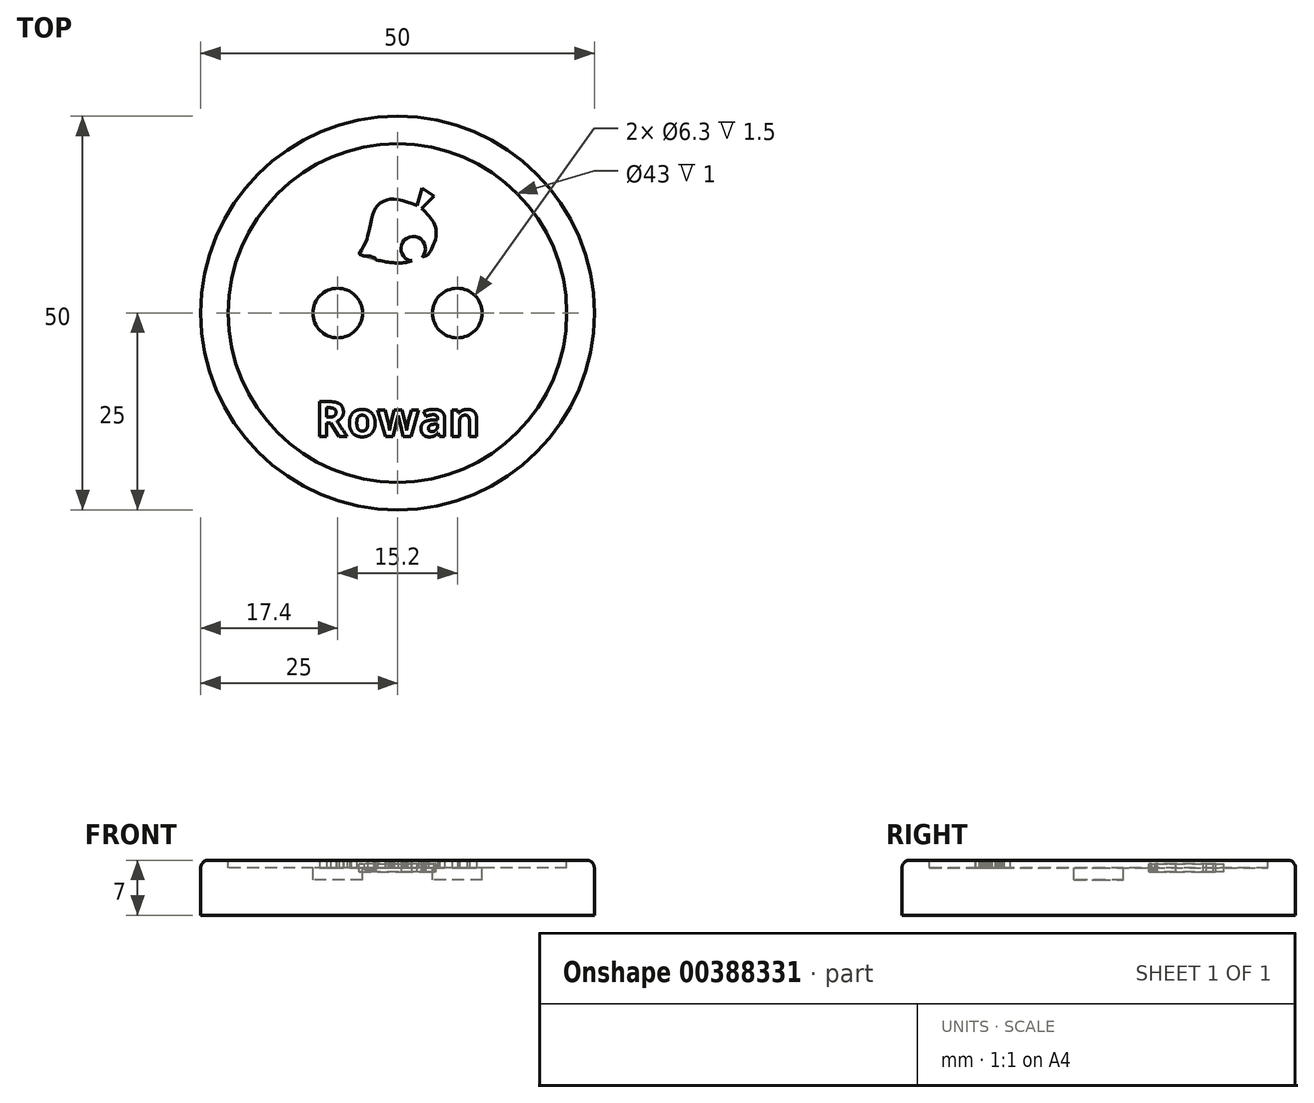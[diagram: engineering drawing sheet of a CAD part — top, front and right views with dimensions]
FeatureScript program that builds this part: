
annotation { "Feature Type Name" : "Feature", "Feature Type Description" : "" }
export const myFeature = defineFeature(function(context is Context, id is Id, definition is map)
    precondition{}
    {
        {
            var Q0;
            Q0=qCreatedBy(makeId("Top.planeOp"),FACE);
            var sketch = newSketch(context, id + "F0", { "sketchPlane" : qUnion([Q0])});
            skCircle(sketch, "E0", {"center": v(0, 0) * mm, "radius": 25 * mm});
            skSolve(sketch);
        }
        {
            var Q0;
            Q0 = qSketchRegion(id + "F0", true);
            extrude(context, id + "F1", {"entities" : qUnion([Q0]), "depth" : 7 * mm});
        }
        {
            var Q0;
            Q0=makeQuery(id+"F1.opExtrude","CAP_FACE",FACE,{"disambiguationData":[OSD([sQuery(id+"F0.wireOp",EDGE,"E0")])],"isStart":false});
            var sketch = newSketch(context, id + "F2", { "sketchPlane" : qUnion([Q0])});
            skLineSegment(sketch, "E1", {"start": v(6.19, 20.35) * mm, "end": v(4.91, 15.94) * mm});
            skLineSegment(sketch, "E2", {"start": v(6.19, 20.35) * mm, "end": v(9.23, 18.39) * mm});
            skFitSpline(sketch, "E3", {"points": [v(4.91, 15.94) * mm, v(0.1, 17.5) * mm, v(-2.94, 17.3) * mm, v(-5, 15.94) * mm, v(-6.27, 13.68) * mm, v(-7.25, 9.46) * mm, v(-7.94, 7) * mm, v(-9.7, 3.57) * mm], "startDerivative": vector(-28.59, 11.34) * mm, "endDerivative": vector(-13.25, -23.76) * mm});
            skFitSpline(sketch, "E4", {"points": [v(-9.7, 3.57) * mm, v(-5.98, 2.3) * mm, v(-1.27, 1.42) * mm, v(1.67, 1.42) * mm, v(3.73, 1.9) * mm], "startDerivative": vector(13.08, -5) * mm, "endDerivative": vector(10.07, 2.94) * mm});
            skFitSpline(sketch, "E5", {"points": [v(3.73, 1.9) * mm, v(2.26, 2.3) * mm, v(1.08, 3.97) * mm, v(1.08, 6.03) * mm, v(2.46, 7.7) * mm, v(4.91, 7.99) * mm, v(6.68, 6.52) * mm, v(7.07, 4.79) * mm, v(6.38, 2.89) * mm], "startDerivative": vector(-14.18, 1.44) * mm, "endDerivative": vector(-7.37, -15.3) * mm});
            skFitSpline(sketch, "E6", {"points": [v(6.38, 2.89) * mm, v(7.76, 3.57) * mm, v(9.23, 6.13) * mm, v(9.82, 9.46) * mm, v(8.64, 12.5) * mm, v(6.09, 15.2) * mm], "startDerivative": vector(9.78, 3.1) * mm, "endDerivative": vector(-12.34, 11.35) * mm});
            skLineSegment(sketch, "E7", {"start": v(6.09, 15.2) * mm, "end": v(9.23, 18.39) * mm});
            skSolve(sketch);
        }
        {
            var Q0;
            Q0 = qSketchRegion(id + "F2", true);
            extrude(context, id + "F3", {"entities" : qUnion([Q0]), "oppositeDirection" : true, "depth" : 3 * mm});
        }
        {
            var Q0;
            Q0=makeQuery(id+"F1.opExtrude","CAP_FACE",FACE,{"disambiguationData":[OSD([sQuery(id+"F0.wireOp",EDGE,"E0")])],"isStart":false});
            var sketch = newSketch(context, id + "F4", { "sketchPlane" : qUnion([Q0])});
            skCircle(sketch, "E8", {"center": v(0, 0) * mm, "radius": 21.5 * mm});
            skSolve(sketch);
        }
        {
            var Q0;
            Q0 = qSketchRegion(id + "F4", true);
            extrude(context, id + "F5", {"entities" : qUnion([Q0]), "operationType" : NewBodyOperationType.REMOVE, "oppositeDirection" : true, "depth" : 1 * mm});
        }
        {
            var Q0;
            Q0=makeQuery(id+"F1.opExtrude","CAP_EDGE",EDGE,{"disambiguationData":[OSD([sQuery(id+"F0.wireOp",EDGE,"E0")])],"isStart":false});
            fillet(context, id + "F6", {"entities" : qUnion([Q0]), "radius" : 1 * mm, "tangentPropagation" : true, "allowEdgeOverflow" : false});
        }
        {
            var Q0;
            Q0=makeQuery(id+"F5.boolean.opBoolean","COPY",FACE,{"derivedFrom":makeQuery(id+"F5.opExtrude","CAP_FACE",FACE,{"disambiguationData":[OSD([sQuery(id+"F4.wireOp",EDGE,"E8")])],"isStart":false})});
            var sketch = newSketch(context, id + "F7", { "sketchPlane" : qUnion([Q0])});
            skText(sketch, "E9", { "text": "Rowan", "fontName": "OpenSans-Bold.ttf"});
            const initialGuessF7  = {"E9": [-0.01047, -0.01567, 1, 0, 0.00445]};
            skSetInitialGuess(sketch, initialGuessF7);
            skSolve(sketch);
        }
        {
            var Q0;
            Q0 = qSketchRegion(id + "F7", true);
            extrude(context, id + "F8", {"entities" : qUnion([Q0]), "operationType" : NewBodyOperationType.ADD, "depth" : 1 * mm});
        }
        {
            var Q0;
            {var subQ0=sQuery(id+"F4.wireOp",EDGE,"E8");Q0=makeQuery(id+"F8.boolean.opBoolean","SPLIT",FACE,{"disambiguationData":[TD([makeQuery(id+"F5.boolean.opBoolean","COPY",FACE,{"derivedFrom":makeQuery(id+"F5.opExtrude","SWEPT_FACE",FACE,{"disambiguationData":[OSD([subQ0])]})})])],"derivedFrom":makeQuery(id+"F5.boolean.opBoolean","COPY",FACE,{"derivedFrom":makeQuery(id+"F5.opExtrude","CAP_FACE",FACE,{"disambiguationData":[OSD([subQ0])],"isStart":false})})});}
            var sketch = newSketch(context, id + "F9", { "sketchPlane" : qUnion([Q0])});
            skCircle(sketch, "E10", {"center": v(-7.6, 0) * mm, "radius": 3.15 * mm});
            skCircle(sketch, "E11.MirrorC", {"center": v(7.6, 0) * mm, "radius": 3.15 * mm});
            skSolve(sketch);
        }
        {
            var Q0;
            Q0 = qSketchRegion(id + "F9", true);
            extrude(context, id + "F10", {"entities" : qUnion([Q0]), "operationType" : NewBodyOperationType.REMOVE, "oppositeDirection" : true, "depth" : 1.5 * mm});
        }
        {
            var Q0;
            Q0=makeQuery(id+"F1.opExtrude","CAP_FACE",FACE,{"disambiguationData":[OSD([sQuery(id+"F0.wireOp",EDGE,"E0")])],"isStart":false});
            var sketch = newSketch(context, id + "F11", { "sketchPlane" : qUnion([Q0])});
            skPoint(sketch, "E12", {"position": v(0, 11.38) * mm});
            skSolve(sketch);
        }
        {
            var Q0;
            Q0=makeQuery(id+"F3.opExtrude","SWEPT_BODY",BODY,{"disambiguationData":[OSD([sQuery(id+"F2.wireOp",EDGE,"E1"),sQuery(id+"F2.wireOp",EDGE,"E2"),sQuery(id+"F2.wireOp",EDGE,"E3"),sQuery(id+"F2.wireOp",EDGE,"E4"),sQuery(id+"F2.wireOp",EDGE,"E5"),sQuery(id+"F2.wireOp",EDGE,"E6"),sQuery(id+"F2.wireOp",EDGE,"E7")])]});
            var Q1;
            Q1=sQuery(id+"F11.wireOp",VERTEX,"E12");
            transform(context, id + "F12", {"entities" : qUnion([Q0]), "transformType" : TransformType.SCALE_UNIFORMLY, "scale" : .5, "scalePoint" : qUnion([Q1]), "makeCopy" : false});
        }
    });
